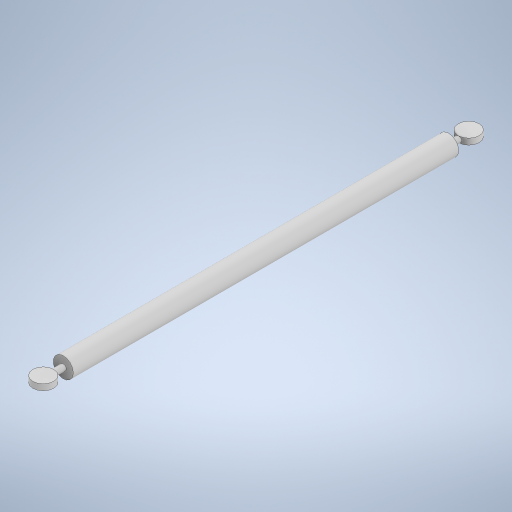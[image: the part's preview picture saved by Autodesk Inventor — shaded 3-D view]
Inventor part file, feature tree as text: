
AUTODESK INVENTOR PART (.ipt)
format: ipt  version: 2023 (Build 270158000, 158)  size: 256,512 bytes
history: native  units: in
note: dims shown in document units (in); Inventor stores cm internally (conversion verified against a paired STEP export)
features: extrude x3, sketch x3, plane x1, mirror x1
ambient origin geometry x8: Origin, YZ Plane, XZ Plane, XY Plane, X Axis, Y Axis, Z Axis, Center Point
bodies: Solid1 (feature_tree)
feature tree (8):
  extrude  "Extrusion1"  Depth=48.0in TaperAngle=0.0deg
  extrude  "Extrusion2"  Depth=0.75in TaperAngle=0.0deg
  extrude  "Extrusion3"  Depth=0.75in
  plane  "Work Plane1"
  mirror  "Mirror1"
  sketch  "Sketch1"  dims[d0=2.5in d1=48.0in d2=0.0in]
  sketch  "Sketch2"  dims[d3=0.75in d4=2.0in d5=0.0in]
  sketch  "Sketch3"  dims[d6=2.5in d7=2.6in d8=0.75in d9=0.0in]
